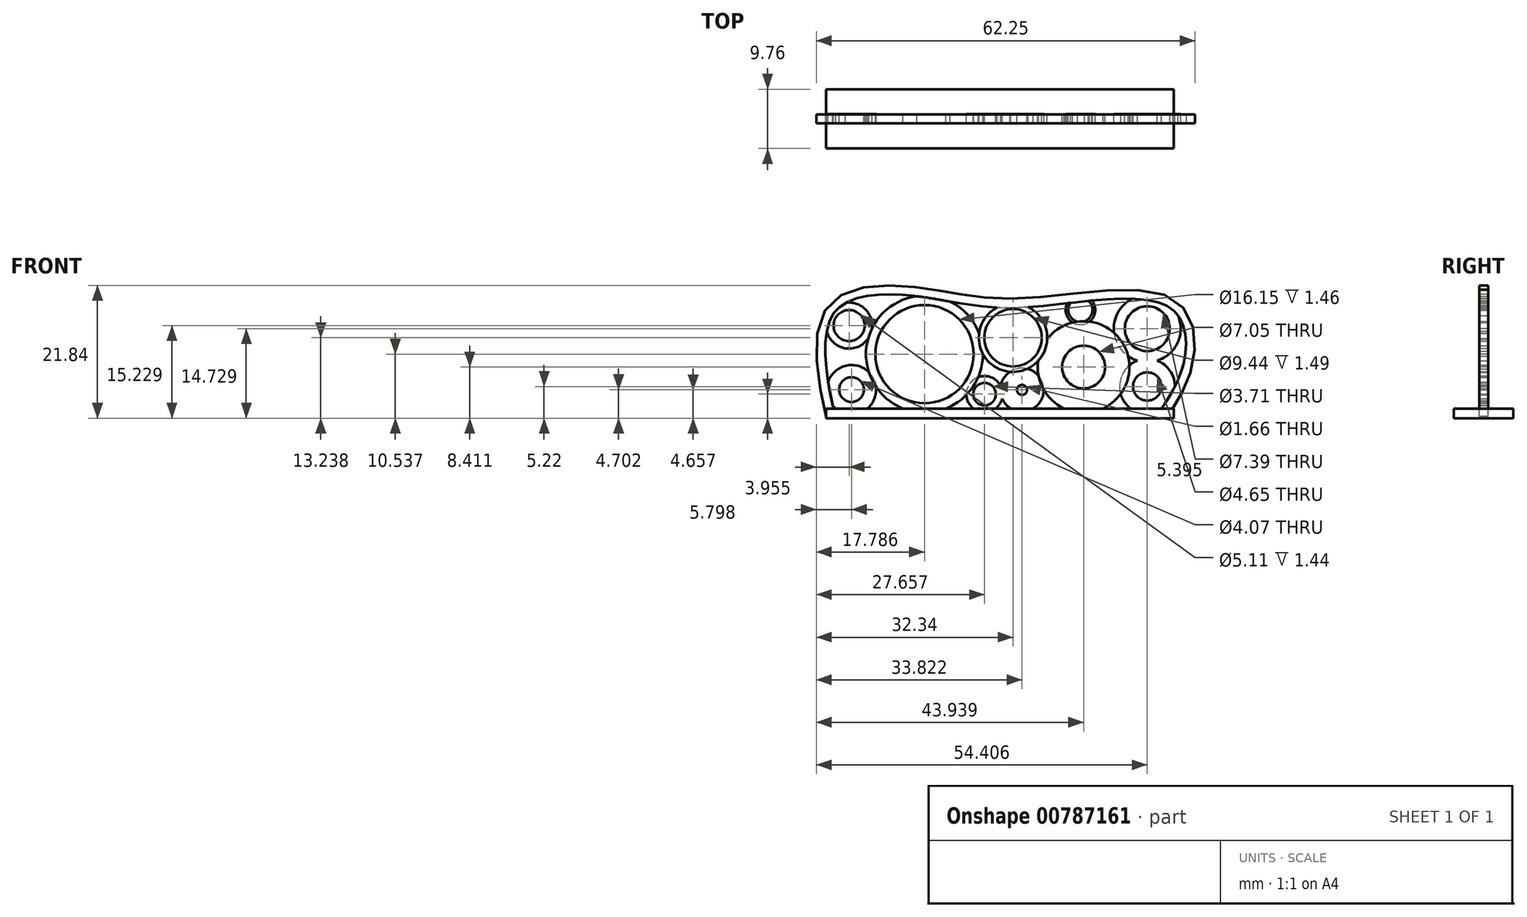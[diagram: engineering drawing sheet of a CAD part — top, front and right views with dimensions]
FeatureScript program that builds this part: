
annotation { "Feature Type Name" : "Feature", "Feature Type Description" : "" }
export const myFeature = defineFeature(function(context is Context, id is Id, definition is map)
    precondition{}
    {
        {
            var Q0;
            Q0=qCreatedBy(makeId("Front.planeOp"),FACE);
            var sketch = newSketch(context, id + "F0", { "sketchPlane" : qUnion([Q0])});
            skFitSpline(sketch, "E0", {"points": [v(-28.54, 0) * mm, v(-28.54, 17.9) * mm, v(-14.68, 20.85) * mm, v(2.13, 18.94) * mm, v(27.2, 19.06) * mm, v(30.17, 8.83) * mm, v(26.14, 0.8) * mm], "startDerivative": vector(-23.6, 98.86) * mm, "endDerivative": vector(-23.3, -30.36) * mm});
            skSolve(sketch);
        }
        {
            var Q0;
            Q0=qCreatedBy(makeId("Top.planeOp"),FACE);
            var sketch = newSketch(context, id + "F1", { "sketchPlane" : qUnion([Q0])});
            skLineSegment(sketch, "E1.bottom", {"start": v(-27.77, 0.83) * mm, "end": v(-29.28, 0.83) * mm});
            skLineSegment(sketch, "E1.top", {"start": v(-27.77, -0.66) * mm, "end": v(-29.28, -0.66) * mm});
            skLineSegment(sketch, "E1.left", {"start": v(-27.77, 0.83) * mm, "end": v(-27.77, -0.66) * mm});
            skLineSegment(sketch, "E1.right", {"start": v(-29.28, 0.83) * mm, "end": v(-29.28, -0.66) * mm});
            skSolve(sketch);
        }
        {
            var Q0;
            Q0=makeQuery(id+"F1.imprint","IMPRINT",FACE,{"disambiguationData":[TD([[makeQuery(id+"F1.imprint","IMPRINT",EDGE,{"derivedFrom":sQuery(id+"F1.wireOp",EDGE,"E1.bottom")}),1.0]])]});
            var Q1;
            Q1=sQuery(id+"F0.wireOp",EDGE,"E0");
            sweep(context, id + "F2", {"profiles" : qUnion([Q0]), "path" : qUnion([Q1])});
        }
        {
            var Q0;
            Q0=qCreatedBy(makeId("Top.planeOp"),FACE);
            var sketch = newSketch(context, id + "F3", { "sketchPlane" : qUnion([Q0])});
            skLineSegment(sketch, "E2.bottom", {"start": v(-29.35, 4.95) * mm, "end": v(27.8, 4.95) * mm});
            skLineSegment(sketch, "E2.top", {"start": v(-29.35, -4.8) * mm, "end": v(27.8, -4.8) * mm});
            skLineSegment(sketch, "E2.left", {"start": v(-29.35, 4.95) * mm, "end": v(-29.35, -4.8) * mm});
            skLineSegment(sketch, "E2.right", {"start": v(27.8, 4.95) * mm, "end": v(27.8, -4.8) * mm});
            skSolve(sketch);
        }
        {
            var Q0;
            Q0=makeQuery(id+"F3.imprint","IMPRINT",FACE,{"disambiguationData":[TD([[makeQuery(id+"F3.imprint","IMPRINT",EDGE,{"derivedFrom":sQuery(id+"F3.wireOp",EDGE,"E2.bottom")}),-1.0]])]});
            extrude(context, id + "F4", {"entities" : qUnion([Q0]), "operationType" : NewBodyOperationType.ADD, "depth" : 1.6 * mm, "offsetDistance" : 25 * mm});
        }
        {
            var Q0;
            Q0=qCreatedBy(makeId("Front.planeOp"),FACE);
            var sketch = newSketch(context, id + "F5", { "sketchPlane" : qUnion([Q0])});
            skCircle(sketch, "E3", {"center": v(-13.15, 10.54) * mm, "radius": 9.61 * mm});
            skCircle(sketch, "E4", {"center": v(-13.15, 10.54) * mm, "radius": 8.08 * mm});
            skSolve(sketch);
        }
        {
            var Q0;
            Q0=makeQuery(id+"F5.imprint","IMPRINT",FACE,{"disambiguationData":[TD([[makeQuery(id+"F5.imprint","IMPRINT",EDGE,{"derivedFrom":sQuery(id+"F5.wireOp",EDGE,"E3")}),1.0]])]});
            extrude(context, id + "F6", {"entities" : qUnion([Q0]), "operationType" : NewBodyOperationType.ADD, "depth" : 0.64 * mm, "offsetDistance" : 25 * mm, "hasSecondDirection" : true, "secondDirectionOppositeDirection" : true, "secondDirectionDepth" : 0.82 * mm});
        }
        {
            var Q0;
            Q0=qCreatedBy(makeId("Front.planeOp"),FACE);
            var sketch = newSketch(context, id + "F7", { "sketchPlane" : qUnion([Q0])});
            skCircle(sketch, "E5", {"center": v(13, 8.41) * mm, "radius": 7.54 * mm});
            skCircle(sketch, "E6", {"center": v(13, 8.41) * mm, "radius": 3.52 * mm});
            skSolve(sketch);
        }
        {
            var Q0;
            Q0 = qSketchRegion(id + "F7", true);
            extrude(context, id + "F8", {"entities" : qUnion([Q0]), "operationType" : NewBodyOperationType.ADD, "depth" : 0.66 * mm, "offsetDistance" : 25 * mm, "hasSecondDirection" : true, "secondDirectionOppositeDirection" : true, "secondDirectionDepth" : 0.79 * mm});
        }
        {
            var Q0;
            Q0=qCreatedBy(makeId("Front.planeOp"),FACE);
            var sketch = newSketch(context, id + "F9", { "sketchPlane" : qUnion([Q0])});
            skCircle(sketch, "E7", {"center": v(1.4, 13.24) * mm, "radius": 5.62 * mm});
            skCircle(sketch, "E8", {"center": v(1.4, 13.24) * mm, "radius": 4.72 * mm});
            skSolve(sketch);
        }
        {
            var Q0;
            Q0=makeQuery(id+"F9.imprint","IMPRINT",FACE,{"disambiguationData":[TD([[makeQuery(id+"F9.imprint","IMPRINT",EDGE,{"derivedFrom":sQuery(id+"F9.wireOp",EDGE,"E7")}),1.0]])]});
            extrude(context, id + "F10", {"entities" : qUnion([Q0]), "operationType" : NewBodyOperationType.ADD, "depth" : 0.67 * mm, "offsetDistance" : 25 * mm, "hasSecondDirection" : true, "secondDirectionOppositeDirection" : true, "secondDirectionDepth" : 0.82 * mm});
        }
        {
            var Q0;
            Q0=qCreatedBy(makeId("Front.planeOp"),FACE);
            var sketch = newSketch(context, id + "F11", { "sketchPlane" : qUnion([Q0])});
            skCircle(sketch, "E9", {"center": v(2.88, 4.66) * mm, "radius": 3.57 * mm});
            skCircle(sketch, "E10", {"center": v(23.47, 14.73) * mm, "radius": 5.5 * mm});
            skCircle(sketch, "E11", {"center": v(23.47, 5.22) * mm, "radius": 4.55 * mm});
            skCircle(sketch, "E12", {"center": v(12.48, 17.82) * mm, "radius": 2.44 * mm});
            skCircle(sketch, "E13", {"center": v(-25.14, 4.7) * mm, "radius": 4.04 * mm});
            skCircle(sketch, "E14", {"center": v(-25.54, 15.23) * mm, "radius": 3.78 * mm});
            skCircle(sketch, "E15", {"center": v(-25.54, 15.23) * mm, "radius": 2.55 * mm});
            skCircle(sketch, "E16", {"center": v(-25.14, 4.7) * mm, "radius": 2.03 * mm});
            skCircle(sketch, "E17", {"center": v(2.88, 4.66) * mm, "radius": 0.83 * mm});
            skCircle(sketch, "E18", {"center": v(12.48, 17.82) * mm, "radius": 1.98 * mm});
            skCircle(sketch, "E19", {"center": v(23.47, 14.73) * mm, "radius": 3.7 * mm});
            skCircle(sketch, "E20", {"center": v(23.47, 5.22) * mm, "radius": 2.33 * mm});
            skCircle(sketch, "E21", {"center": v(-3.28, 3.95) * mm, "radius": 2.98 * mm});
            skCircle(sketch, "E22", {"center": v(-3.28, 3.95) * mm, "radius": 1.86 * mm});
            skSolve(sketch);
        }
        {
            var Q0;
            Q0 = qSketchRegion(id + "F11", true);
            extrude(context, id + "F12", {"entities" : qUnion([Q0]), "operationType" : NewBodyOperationType.ADD, "depth" : 0.6 * mm, "offsetDistance" : 25 * mm, "hasSecondDirection" : true, "secondDirectionOppositeDirection" : true, "secondDirectionDepth" : 0.84 * mm});
        }
    });
